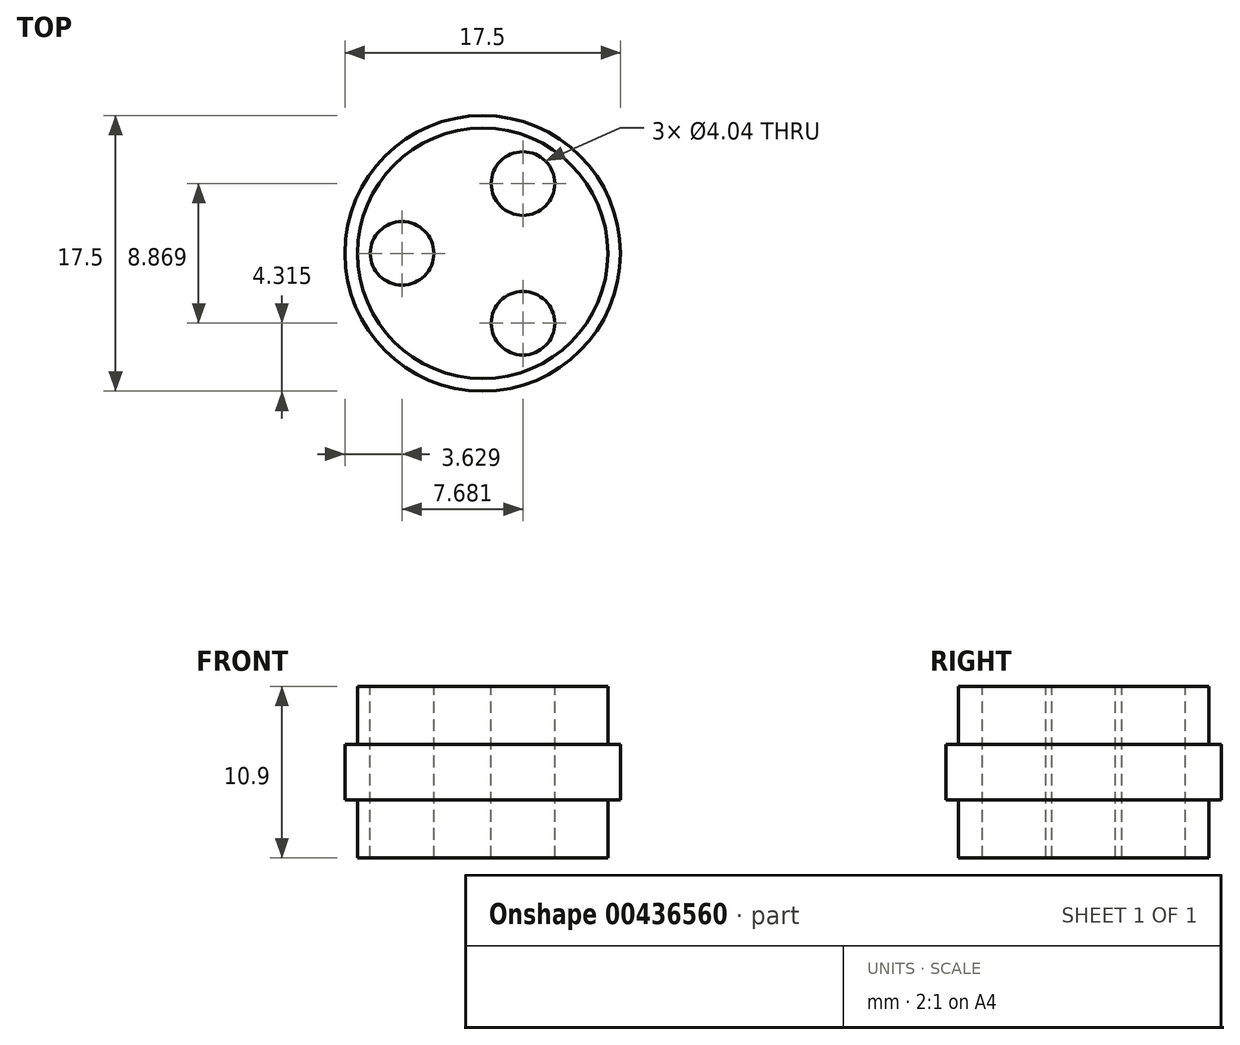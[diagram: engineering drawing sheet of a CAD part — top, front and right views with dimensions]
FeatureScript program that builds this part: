
annotation { "Feature Type Name" : "Feature", "Feature Type Description" : "" }
export const myFeature = defineFeature(function(context is Context, id is Id, definition is map)
    precondition{}
    {
        {
            var Q0;
            Q0=qCreatedBy(makeId("Top.planeOp"),FACE);
            var sketch = newSketch(context, id + "F0", { "sketchPlane" : qUnion([Q0])});
            skCircle(sketch, "E0", {"center": v(0, 0) * mm, "radius": 7.95 * mm});
            skSolve(sketch);
        }
        {
            var Q0;
            Q0 = qSketchRegion(id + "F0", true);
            extrude(context, id + "F1", {"entities" : qUnion([Q0]), "depth" : 3.7 * mm});
        }
        {
            var Q0;
            Q0=makeQuery(id+"F1.opExtrude","CAP_FACE",FACE,{"disambiguationData":[OSD([sQuery(id+"F0.wireOp",EDGE,"E0")])],"isStart":false});
            var sketch = newSketch(context, id + "F2", { "sketchPlane" : qUnion([Q0])});
            skCircle(sketch, "E1", {"center": v(0, 0) * mm, "radius": 8.75 * mm});
            skSolve(sketch);
        }
        {
            var Q0;
            Q0 = qSketchRegion(id + "F2", true);
            extrude(context, id + "F3", {"entities" : qUnion([Q0]), "operationType" : NewBodyOperationType.ADD, "depth" : 3.5 * mm});
        }
        {
            var Q0;
            Q0=makeQuery(id+"F3.opExtrude","CAP_FACE",FACE,{"disambiguationData":[OSD([sQuery(id+"F2.wireOp",EDGE,"E1")])],"isStart":false});
            var sketch = newSketch(context, id + "F4", { "sketchPlane" : qUnion([Q0])});
            skCircle(sketch, "E2", {"center": v(0, 0) * mm, "radius": 7.95 * mm});
            skSolve(sketch);
        }
        {
            var Q0;
            Q0 = qSketchRegion(id + "F4", true);
            extrude(context, id + "F5", {"entities" : qUnion([Q0]), "operationType" : NewBodyOperationType.ADD, "depth" : 3.7 * mm});
        }
        {
            var Q0;
            Q0=makeQuery(id+"F5.opExtrude","CAP_FACE",FACE,{"disambiguationData":[OSD([sQuery(id+"F4.wireOp",EDGE,"E2")])],"isStart":false});
            var sketch = newSketch(context, id + "F6", { "sketchPlane" : qUnion([Q0])});
            skCircle(sketch, "E3", {"center": v(0, 0) * mm, "radius": 5.12 * mm, "construction": true});
            skCircle(sketch, "E4", {"center": v(-5.12, 0) * mm, "radius": 2.02 * mm});
            skCircle(sketch, "E5.1.0", {"center": v(2.56, -4.43) * mm, "radius": 2.02 * mm});
            skCircle(sketch, "E5.2.0", {"center": v(2.56, 4.43) * mm, "radius": 2.02 * mm});
            skSolve(sketch);
        }
        {
            var Q0;
            Q0 = qSketchRegion(id + "F6", true);
            extrude(context, id + "F7", {"entities" : qUnion([Q0]), "operationType" : NewBodyOperationType.REMOVE, "endBound" : BoundingType.THROUGH_ALL, "oppositeDirection" : true, "depth" : 25 * mm});
        }
    });
